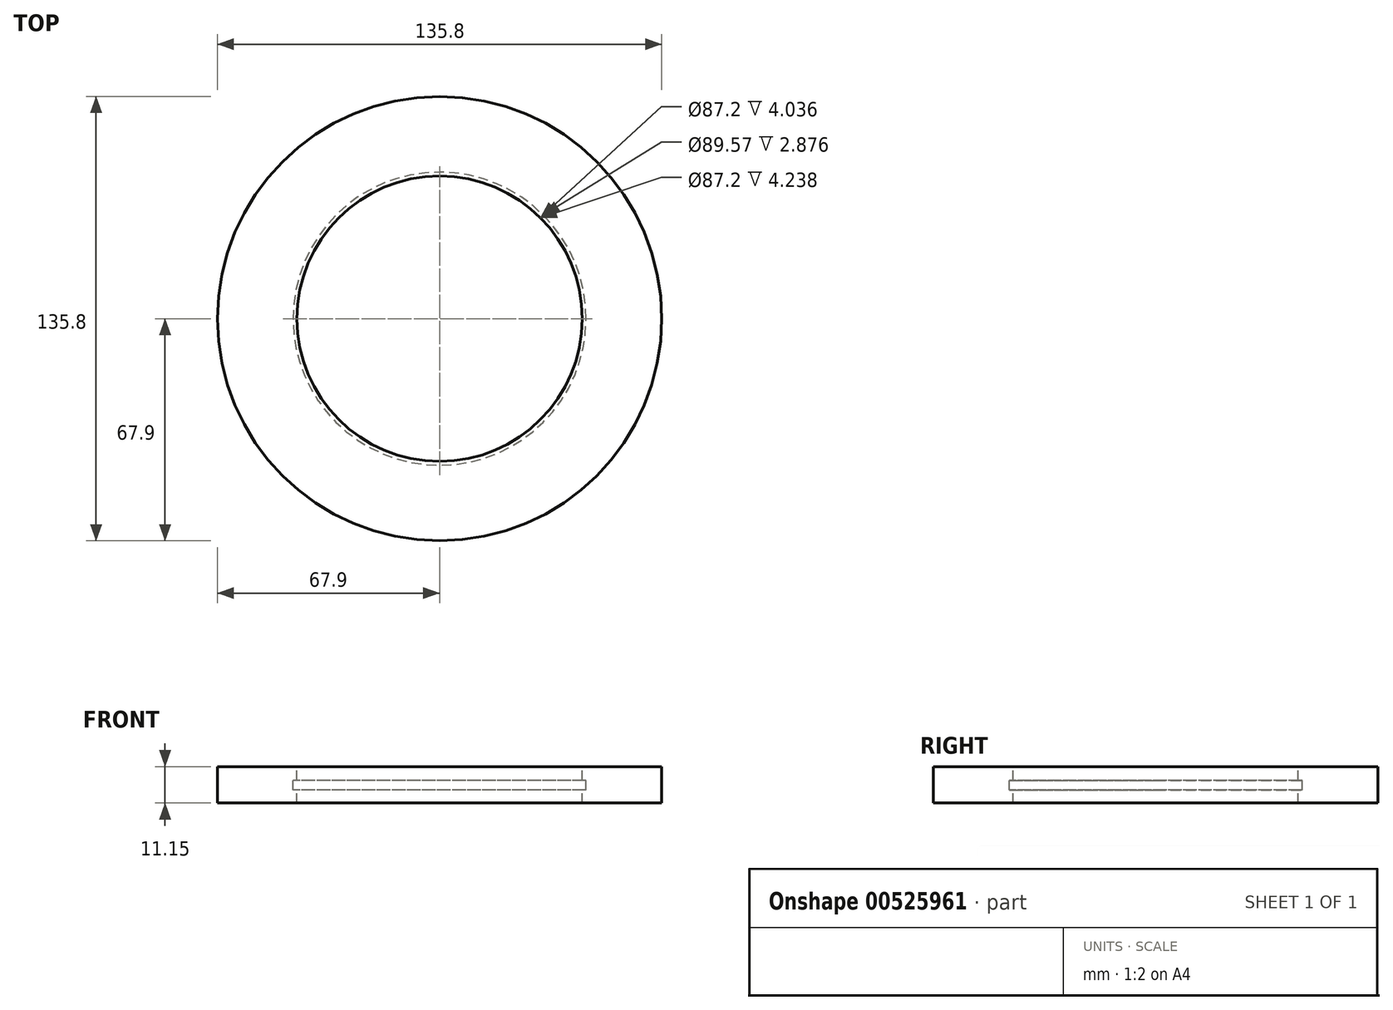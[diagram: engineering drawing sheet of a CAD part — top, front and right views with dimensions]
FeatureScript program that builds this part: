
annotation { "Feature Type Name" : "Feature", "Feature Type Description" : "" }
export const myFeature = defineFeature(function(context is Context, id is Id, definition is map)
    precondition{}
    {
        {
            var Q0;
            Q0=qCreatedBy(makeId("Front.planeOp"),FACE);
            var sketch = newSketch(context, id + "F0", { "sketchPlane" : qUnion([Q0])});
            skLineSegment(sketch, "E0", {"start": v(0, 0) * mm, "end": v(-25.63, 0) * mm});
            skLineSegment(sketch, "E1", {"start": v(-25.63, 0) * mm, "end": v(-25.63, 11.15) * mm});
            skLineSegment(sketch, "E2", {"start": v(-25.63, 11.15) * mm, "end": v(0, 11.15) * mm});
            skLineSegment(sketch, "E3", {"start": v(0, 11.15) * mm, "end": v(0, 0) * mm});
            skLineSegment(sketch, "E4", {"start": v(-43.6, 0) * mm, "end": v(-67.9, 0) * mm});
            skLineSegment(sketch, "E5", {"start": v(-67.9, 0) * mm, "end": v(-67.9, 11.15) * mm});
            skLineSegment(sketch, "E6", {"start": v(-67.9, 11.15) * mm, "end": v(-43.6, 11.15) * mm});
            skLineSegment(sketch, "E7", {"start": v(-43.6, 11.15) * mm, "end": v(-43.6, 6.91) * mm});
            skLineSegment(sketch, "E8", {"start": v(-43.6, 6.91) * mm, "end": v(-44.78, 6.91) * mm});
            skLineSegment(sketch, "E9", {"start": v(-44.78, 6.91) * mm, "end": v(-44.78, 4.04) * mm});
            skLineSegment(sketch, "E10", {"start": v(-44.78, 4.04) * mm, "end": v(-43.6, 4.04) * mm});
            skLineSegment(sketch, "E11", {"start": v(-43.6, 4.04) * mm, "end": v(-43.6, 0) * mm});
            skSolve(sketch);
        }
        {
            var Q0;
            Q0=makeQuery(id+"F0.imprint","IMPRINT",FACE,{"disambiguationData":[TD([[makeQuery(id+"F0.imprint","IMPRINT",EDGE,{"derivedFrom":sQuery(id+"F0.wireOp",EDGE,"E4")}),-1.0]])]});
            var Q1;
            Q1=sQuery(id+"F0.wireOp",EDGE,"E3");
            revolve(context, id + "F1", {"entities" : qUnion([Q0]), "axis" : qUnion([Q1]), "revolveType" : RevolveType.FULL});
        }
    });
